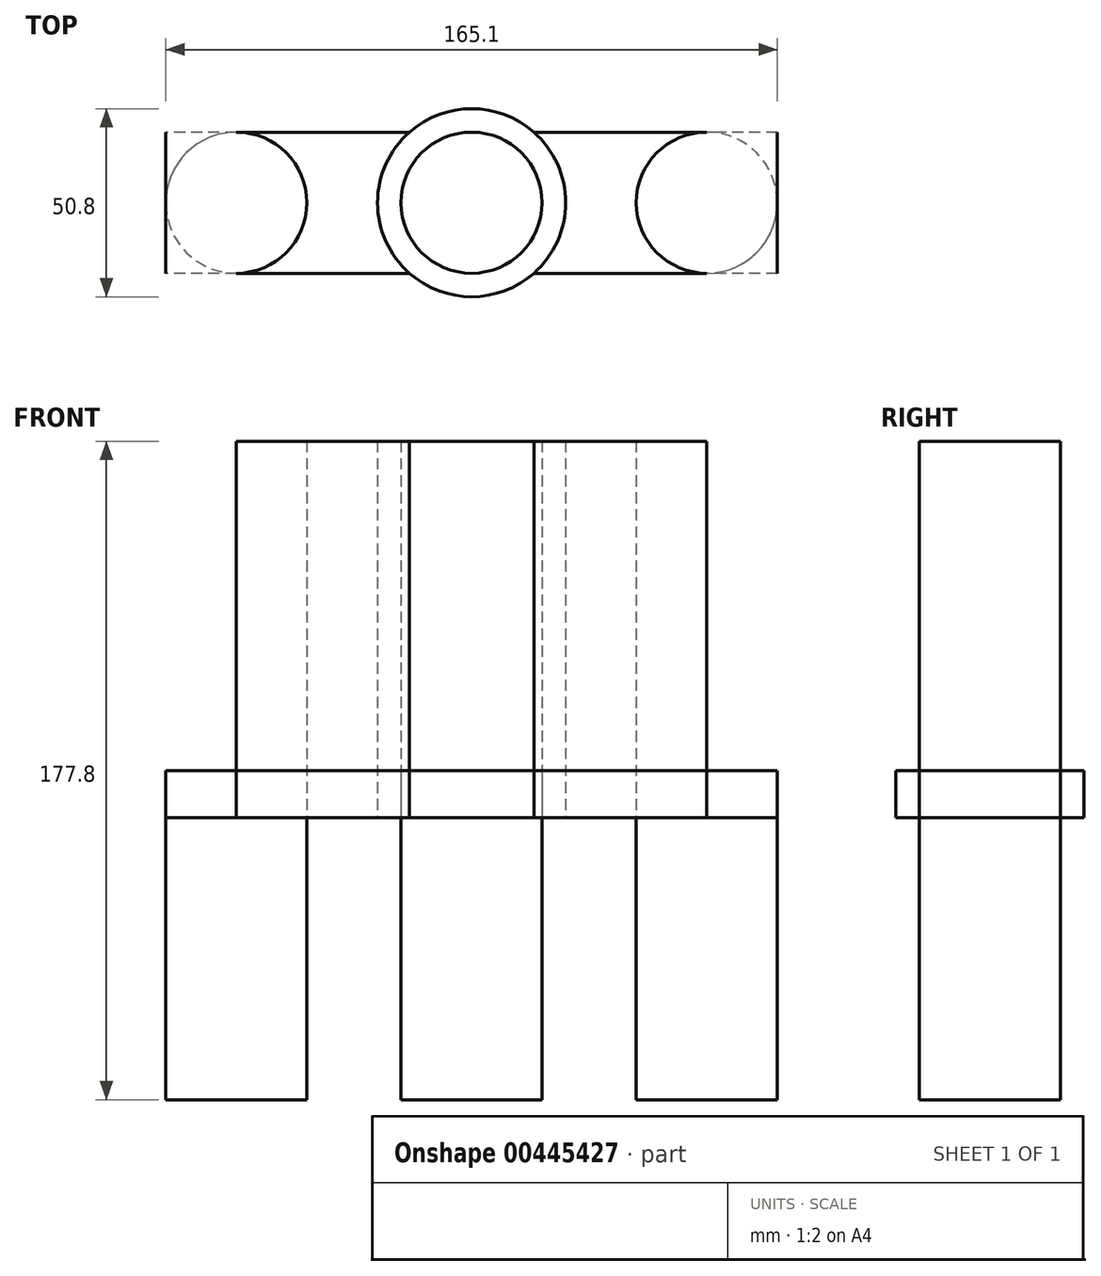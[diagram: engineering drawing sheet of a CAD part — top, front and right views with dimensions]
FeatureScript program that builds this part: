
annotation { "Feature Type Name" : "Feature", "Feature Type Description" : "" }
export const myFeature = defineFeature(function(context is Context, id is Id, definition is map)
    precondition{}
    {
        {
            var Q0;
            Q0=qCreatedBy(makeId("Top.planeOp"),FACE);
            var sketch = newSketch(context, id + "F0", { "sketchPlane" : qUnion([Q0])});
            skLineSegment(sketch, "E0.bottom", {"start": v(82.55, 19.05) * mm, "end": v(-82.55, 19.05) * mm});
            skLineSegment(sketch, "E0.top", {"start": v(82.55, -19.05) * mm, "end": v(-82.55, -19.05) * mm});
            skLineSegment(sketch, "E0.left", {"start": v(82.55, 19.05) * mm, "end": v(82.55, -19.05) * mm});
            skLineSegment(sketch, "E0.right", {"start": v(-82.55, 19.05) * mm, "end": v(-82.55, -19.05) * mm});
            skPoint(sketch, "E0.middle", {"position": v(0, 0) * mm});
            skCircle(sketch, "E1", {"center": v(0, 0) * mm, "radius": 19.05 * mm});
            skCircle(sketch, "E2", {"center": v(-63.5, 0) * mm, "radius": 19.05 * mm});
            skCircle(sketch, "E3", {"center": v(63.5, 0) * mm, "radius": 19.05 * mm});
            skCircle(sketch, "E4", {"center": v(0, 0) * mm, "radius": 25.4 * mm});
            skSolve(sketch);
        }
        {
            var Q0;
            Q0 = qSketchRegion(id + "F0", true);
            extrude(context, id + "F1", {"entities" : qUnion([Q0]), "depth" : 12.7 * mm});
        }
        {
            var Q0;
            {var subQ0=sQuery(id+"F0.wireOp",EDGE,"E2");var subQ1=makeQuery(id+"F0.imprint","INTERSECT",VERTEX,{"derivedFrom":[sQuery(id+"F0.wireOp",EDGE,"E0.bottom"),subQ0]});Q0=makeQuery(id+"F0.imprint","IMPRINT",FACE,{"disambiguationData":[TD([[makeQuery(id+"F0.imprint","IMPRINT",EDGE,{"disambiguationData":[TD([[subQ1,-1.0]])],"derivedFrom":subQ0}),1.0]])]});}
            var Q1;
            {var subQ0=sQuery(id+"F0.wireOp",EDGE,"E1");var subQ1=makeQuery(id+"F0.imprint","INTERSECT",VERTEX,{"derivedFrom":[sQuery(id+"F0.wireOp",EDGE,"E0.bottom"),subQ0]});Q1=makeQuery(id+"F0.imprint","IMPRINT",FACE,{"disambiguationData":[TD([[makeQuery(id+"F0.imprint","IMPRINT",EDGE,{"disambiguationData":[TD([[subQ1,-1.0]])],"derivedFrom":subQ0}),1.0]])]});}
            var Q2;
            {var subQ0=sQuery(id+"F0.wireOp",EDGE,"E3");var subQ1=makeQuery(id+"F0.imprint","INTERSECT",VERTEX,{"derivedFrom":[sQuery(id+"F0.wireOp",EDGE,"E0.bottom"),subQ0]});Q2=makeQuery(id+"F0.imprint","IMPRINT",FACE,{"disambiguationData":[TD([[makeQuery(id+"F0.imprint","IMPRINT",EDGE,{"disambiguationData":[TD([[subQ1,1.0]])],"derivedFrom":subQ0}),1.0]])]});}
            extrude(context, id + "F2", {"entities" : qUnion([Q0, Q1, Q2]), "operationType" : NewBodyOperationType.ADD, "oppositeDirection" : true, "depth" : 76.2 * mm});
        }
        {
            var Q0;
            {var subQ0=sQuery(id+"F0.wireOp",EDGE,"E4");var subQ1=sQuery(id+"F0.wireOp",EDGE,"E0.bottom");var subQ2=makeQuery(id+"F0.imprint","INTERSECT",VERTEX,{"disambiguationData":[OD(1.0)],"derivedFrom":[subQ1,subQ0]});Q0=makeQuery(id+"F0.imprint","IMPRINT",FACE,{"disambiguationData":[TD([[makeQuery(id+"F0.imprint","IMPRINT",EDGE,{"disambiguationData":[TD([[subQ2,1.0]])],"derivedFrom":subQ1}),1.0]])]});}
            var Q1;
            {var subQ0=sQuery(id+"F0.wireOp",EDGE,"E1");var subQ1=makeQuery(id+"F0.imprint","INTERSECT",VERTEX,{"derivedFrom":[sQuery(id+"F0.wireOp",EDGE,"E0.bottom"),subQ0]});Q1=makeQuery(id+"F0.imprint","IMPRINT",FACE,{"disambiguationData":[TD([[makeQuery(id+"F0.imprint","IMPRINT",EDGE,{"disambiguationData":[TD([[subQ1,-1.0]])],"derivedFrom":subQ0}),1.0]])]});}
            var Q2;
            {var subQ0=sQuery(id+"F0.wireOp",EDGE,"E4");var subQ1=sQuery(id+"F0.wireOp",EDGE,"E0.top");var subQ2=makeQuery(id+"F0.imprint","INTERSECT",VERTEX,{"disambiguationData":[OD(0.0)],"derivedFrom":[subQ1,subQ0]});Q2=makeQuery(id+"F0.imprint","IMPRINT",FACE,{"disambiguationData":[TD([[makeQuery(id+"F0.imprint","IMPRINT",EDGE,{"disambiguationData":[TD([[subQ2,-1.0]])],"derivedFrom":subQ1}),1.0]])]});}
            var Q3;
            {var subQ0=sQuery(id+"F0.wireOp",EDGE,"E4");var subQ1=sQuery(id+"F0.wireOp",EDGE,"E0.bottom");var subQ2=makeQuery(id+"F0.imprint","INTERSECT",VERTEX,{"disambiguationData":[OD(0.0)],"derivedFrom":[subQ1,subQ0]});Q3=makeQuery(id+"F0.imprint","IMPRINT",FACE,{"disambiguationData":[TD([[makeQuery(id+"F0.imprint","IMPRINT",EDGE,{"disambiguationData":[TD([[subQ2,-1.0]])],"derivedFrom":subQ1}),1.0]])]});}
            var Q4;
            {var subQ0=sQuery(id+"F0.wireOp",EDGE,"E4");var subQ1=sQuery(id+"F0.wireOp",EDGE,"E0.bottom");var subQ2=makeQuery(id+"F0.imprint","INTERSECT",VERTEX,{"disambiguationData":[OD(0.0)],"derivedFrom":[subQ1,subQ0]});Q4=makeQuery(id+"F0.imprint","IMPRINT",FACE,{"disambiguationData":[TD([[makeQuery(id+"F0.imprint","IMPRINT",EDGE,{"disambiguationData":[TD([[subQ2,-1.0]])],"derivedFrom":subQ1}),-1.0]])]});}
            extrude(context, id + "F3", {"entities" : qUnion([Q0, Q1, Q2, Q3, Q4]), "depth" : 101.6 * mm});
        }
    });
